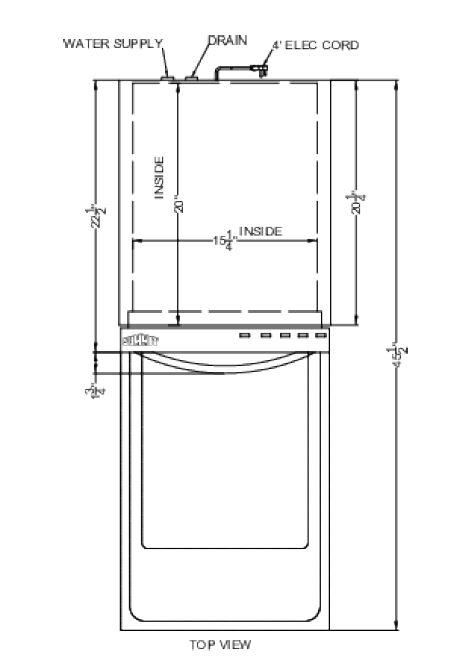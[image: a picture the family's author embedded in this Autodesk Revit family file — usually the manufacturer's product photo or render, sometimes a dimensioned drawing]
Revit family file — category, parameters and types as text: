
# Revit family: QF_Summit_DW185SSADA_Dishwasher
name_source: partatom
category: Specialty Equipment
units: mm (PartAtom-declared; Revit-internal decimal feet)

## family parameters
Always vertical = Yes
Cut with Voids When Loaded = No
Part Type = Normal
Room Calculation Point = No
Round Connector Dimension = Use Diameter
Shared = No
Work Plane-Based = No

## types (1)
- QF_Summit_DW185SSADA_Dishwasher
    Apparent Power = 1380 VA
    Cold Water Connection Height = 0"
    Cold Water Flow = 0 GPM
    Cold Water Maximum Pressure = 0.00 psi
    Cold Water Minimum Pressure = 0.00 psi
    Cold Water RI Height = 0"
    Cold Water Size = 1"
    Cold Water Temperature Recommended = -460 °F
    Conn Conduit = Yes
    Cycle = 60 Hz
    Default Elevation = 0"
    Depth = 24 1/4"
    Description = Dishwasher
    Elec Conn Connection Height = 0"
    Elec Conn RI Height = 0"
    FL Amps = 12 A
    Foodservice Equipment Identifier = Yes
    Identify Quantity as Lot = Yes
    Indirect Waste Connection Height = 0"
    Indirect Waste Flow = 0 GPM
    Indirect Waste Size = 1"
    Length = 17 1/2"
    Manufacturer = Summit
    Max Overcurrent Protection = 0 A
    Min Ckt Ampacity = 0 A
    Model = DW185SSADA
    Number of Poles = 1
    Phase = 1
    Volts = 115 V
    Waste Water Discharge Temperature = -460 °F
    Watts = 1380 W
    Weight in Pounds = 95

## geometry (parser evidence)
native form markers: Blend x16, Sweep x11
no freeform markers — native parametric forms only
